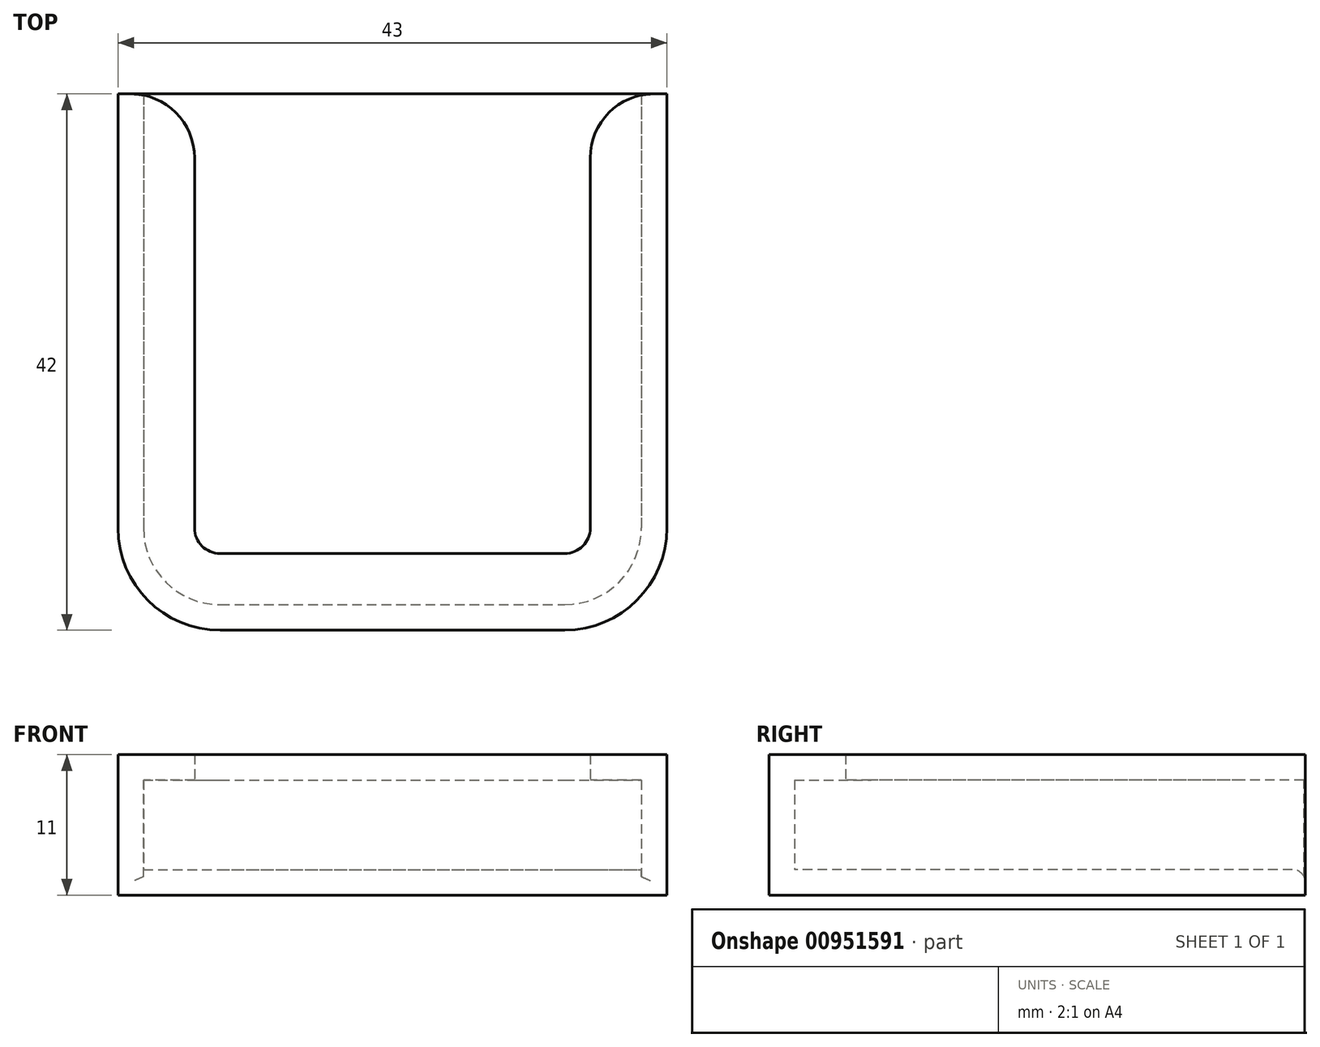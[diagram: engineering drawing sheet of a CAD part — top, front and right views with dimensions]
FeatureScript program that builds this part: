
annotation { "Feature Type Name" : "Feature", "Feature Type Description" : "" }
export const myFeature = defineFeature(function(context is Context, id is Id, definition is map)
    precondition{}
    {
        {
            var Q0;
            Q0=qCreatedBy(makeId("Top.planeOp"),FACE);
            var sketch = newSketch(context, id + "F0", { "sketchPlane" : qUnion([Q0])});
            skLineSegment(sketch, "E0.bottom", {"start": v(-287.64, 300) * mm, "end": v(287.64, 300) * mm});
            skLineSegment(sketch, "E0.top", {"start": v(-287.64, -300) * mm, "end": v(287.64, -300) * mm});
            skLineSegment(sketch, "E0.left", {"start": v(-287.64, 300) * mm, "end": v(-287.64, -300) * mm});
            skLineSegment(sketch, "E0.right", {"start": v(287.64, 300) * mm, "end": v(287.64, -300) * mm});
            skPoint(sketch, "E0.middle", {"position": v(0, 0) * mm});
            skLineSegment(sketch, "E1.bottom", {"start": v(-19.5, 20) * mm, "end": v(19.5, 20) * mm});
            skLineSegment(sketch, "E1.top", {"start": v(-13.5, -20) * mm, "end": v(13.5, -20) * mm});
            skLineSegment(sketch, "E1.left", {"start": v(-19.5, 20) * mm, "end": v(-19.5, -14) * mm});
            skLineSegment(sketch, "E1.right", {"start": v(19.5, 20) * mm, "end": v(19.5, -14) * mm});
            skPoint(sketch, "E2.visualSharp", {"position": v(-19.5, -20) * mm});
            skArc(sketch, "E2.filletArc", {"start": v(-19.5, -14) * mm, "mid": v(-17.74, -18.24) * mm, "end": v(-13.5, -20) * mm});
            skPoint(sketch, "E3.visualSharp", {"position": v(19.5, -20) * mm});
            skArc(sketch, "E3.filletArc", {"start": v(13.5, -20) * mm, "mid": v(17.74, -18.24) * mm, "end": v(19.5, -14) * mm});
            skLineSegment(sketch, "E4.0", {"start": v(21.5, 20) * mm, "end": v(21.5, -14) * mm});
            skLineSegment(sketch, "E4.1", {"start": v(-21.5, 20) * mm, "end": v(-21.5, -14) * mm});
            skArc(sketch, "E4.2", {"start": v(-21.5, -14) * mm, "mid": v(-19.16, -19.66) * mm, "end": v(-13.5, -22) * mm});
            skLineSegment(sketch, "E4.3", {"start": v(-13.5, -22) * mm, "end": v(13.5, -22) * mm});
            skArc(sketch, "E4.4", {"start": v(13.5, -22) * mm, "mid": v(19.16, -19.66) * mm, "end": v(21.5, -14) * mm});
            skLineSegment(sketch, "E5.0", {"start": v(15.5, 20) * mm, "end": v(15.5, -14) * mm});
            skLineSegment(sketch, "E5.1", {"start": v(-15.5, 20) * mm, "end": v(-15.5, -14) * mm});
            skArc(sketch, "E5.2", {"start": v(-15.5, -14) * mm, "mid": v(-14.91, -15.41) * mm, "end": v(-13.5, -16) * mm});
            skLineSegment(sketch, "E5.3", {"start": v(-13.5, -16) * mm, "end": v(13.5, -16) * mm});
            skArc(sketch, "E5.4", {"start": v(13.5, -16) * mm, "mid": v(14.91, -15.41) * mm, "end": v(15.5, -14) * mm});
            skLineSegment(sketch, "E6", {"start": v(-21.5, 20) * mm, "end": v(-19.5, 20) * mm});
            skLineSegment(sketch, "E7", {"start": v(19.5, 20) * mm, "end": v(21.5, 20) * mm});
            skSolve(sketch);
        }
        {
            var Q0;
            Q0=makeQuery(id+"F0.imprint","IMPRINT",FACE,{"disambiguationData":[TD([[makeQuery(id+"F0.imprint","IMPRINT",EDGE,{"derivedFrom":sQuery(id+"F0.wireOp",EDGE,"E1.top")}),-1.0]])]});
            var Q1;
            {var subQ1=sQuery(id+"F0.wireOp",EDGE,"E5.0");Q1=makeQuery(id+"F0.imprint","IMPRINT",FACE,{"disambiguationData":[TD([[makeQuery(id+"F0.imprint","IMPRINT",EDGE,{"derivedFrom":subQ1}),-1.0]])]});}
            var Q2;
            Q2=makeQuery(id+"F0.imprint","IMPRINT",FACE,{"disambiguationData":[TD([[makeQuery(id+"F0.imprint","IMPRINT",EDGE,{"derivedFrom":sQuery(id+"F0.wireOp",EDGE,"E1.top")}),1.0]])]});
            extrude(context, id + "F1", {"entities" : qUnion([Q0, Q1, Q2]), "oppositeDirection" : true, "depth" : 2 * mm, "offsetDistance" : 25 * mm});
        }
        {
            var Q0;
            Q0=makeQuery(id+"F0.imprint","IMPRINT",FACE,{"disambiguationData":[TD([[makeQuery(id+"F0.imprint","IMPRINT",EDGE,{"derivedFrom":sQuery(id+"F0.wireOp",EDGE,"E1.top")}),-1.0]])]});
            extrude(context, id + "F2", {"entities" : qUnion([Q0]), "operationType" : NewBodyOperationType.ADD, "depth" : 7 * mm, "offsetDistance" : 25 * mm});
        }
        {
            var Q0;
            Q0=makeQuery(id+"F0.imprint","IMPRINT",FACE,{"disambiguationData":[TD([[makeQuery(id+"F0.imprint","IMPRINT",EDGE,{"derivedFrom":sQuery(id+"F0.wireOp",EDGE,"E1.top")}),1.0]])]});
            var Q1;
            Q1=makeQuery(id+"F0.imprint","IMPRINT",FACE,{"disambiguationData":[TD([[makeQuery(id+"F0.imprint","IMPRINT",EDGE,{"derivedFrom":sQuery(id+"F0.wireOp",EDGE,"E1.top")}),-1.0]])]});
            extrude(context, id + "F3", {"entities" : qUnion([Q0, Q1]), "operationType" : NewBodyOperationType.ADD, "depth" : 9 * mm, "offsetDistance" : 25 * mm, "hasSecondDirection" : true, "secondDirectionOppositeDirection" : false, "secondDirectionDepth" : 7 * mm});
        }
        {
            var Q0;
            Q0=makeQuery(id+"F3.opExtrude","SWEPT_EDGE",EDGE,{"disambiguationData":[OSD([sQuery(id+"F0.wireOp",EDGE,"E1.bottom"),sQuery(id+"F0.wireOp",EDGE,"E5.1")])]});
            var Q1;
            Q1=makeQuery(id+"F3.opExtrude","SWEPT_EDGE",EDGE,{"disambiguationData":[OSD([sQuery(id+"F0.wireOp",EDGE,"E1.bottom"),sQuery(id+"F0.wireOp",EDGE,"E5.0")])]});
            fillet(context, id + "F4", {"entities" : qUnion([Q0, Q1]), "radius" : 5 * mm, "tangentPropagation" : true, "allowEdgeOverflow" : false});
        }
        {
            var Q0;
            Q0=makeQuery(id+"F1.opExtrude","CAP_EDGE",EDGE,{"disambiguationData":[OSD([sQuery(id+"F0.wireOp",EDGE,"E1.bottom"),sQuery(id+"F0.wireOp",EDGE,"E6"),sQuery(id+"F0.wireOp",EDGE,"E7")])],"isStart":true});
            fillet(context, id + "F5", {"entities" : qUnion([Q0]), "radius" : 1 * mm, "tangentPropagation" : true, "allowEdgeOverflow" : false});
        }
    });
